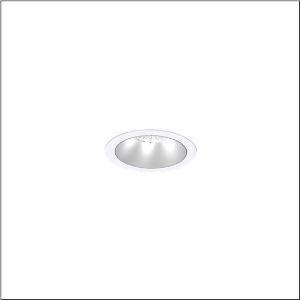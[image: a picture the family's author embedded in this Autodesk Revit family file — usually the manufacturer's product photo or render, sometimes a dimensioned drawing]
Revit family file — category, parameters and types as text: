
# Revit family: lunis_21_m_51db19ec91c
name_source: partatom
category: Lighting Fixtures
units: mm (PartAtom-declared; Revit-internal decimal feet)

## family parameters
Cut with Voids When Loaded = No
Host = Face
Light Source = No
Part Type = Normal
Room Calculation Point = No
Round Connector Dimension = Use Diameter
Shared = No

## types (1)
- --- (1 x LED, 3750 lm, 25.5 W, 4000K)
    Apparent Load = 26 VA
    CIE Flux Codes = 95 100 100 100 100
    Color Rendering = 80
    Color Temperature = 4000K
    Default Elevation = 1800 mm
    Description = Lunis 21,  M, downlight, light control with lens, of PMMA, anti glare with reflector, of PC, matt, light emission: direct distribution, LED rated luminous flux: 1.730lm, light colour: 830/840/865, with terminal, 5-pole, mains connection: 220..240V, AC/DC, 0/50..60Hz, housing, round, of diecast aluminium, traffic white (RAL 9016), diameter: 115mm, clamping range: 1..40mm, protection rating (complete): IP20, protection rating (on room side): IP54, insulation class (complete): insulation class II (safety insulation), certification: CE, impact resistance: IK03, packaging unit: 1 piece
    Height = 0 mm  [stored 0 ft]
    Lamp = 1 x LED
    Lamp Light Flux = 3750 lm
    Lamp Power = 25.5 W
    Lamp count = 1
    Length = 115 mm
    Luminous efficacy = 147 lm/W
    Manufacturer = Siteco
    ModVariant = No
    Model = 51DB19EC91C
    Mounting Place = Ceiling
    Mounting Type = Recessed
    Number of Poles = 1
    OnlyDefault = Yes
    Power Factor = 1
    Product Name = Lunis 21 M
    Product group = downlight
    ProductGroupID = 400
    Protection Class = Protection class II
    Protection Degree = IP 20
    RLX_Detail_Level = 1
    RLX_Emergency_Light_Flux = 0 lm
    RLX_Emergency_Type = 0
    RLX_Emergency_Type_DB = No
    RlxData = <blob elided: 11393 chars, md5=4b0a1674>
    Socket = socket
    Standby Power = 0 W
    System Light Flux = 3750 lm
    System Power = 26 W
    Type Comments = individual setting: colour temperature 4000K, luminous flux: 100 % | (ON | ON | OFF | OFF) | 700 mA
    Type Image = l_1290856.jpg
    URL = http://relux.com
    VarID = @adj_017645
    Voltage = 0 V
    Weight = 0.00 kg
    Width = 0 mm  [stored 0 ft]

note: [stored X ft] marks values corroborated as IEEE doubles in the binary element streams (Revit-internal decimal feet)

## geometry (parser evidence)
native form markers: Sweep x9
no freeform markers — native parametric forms only
